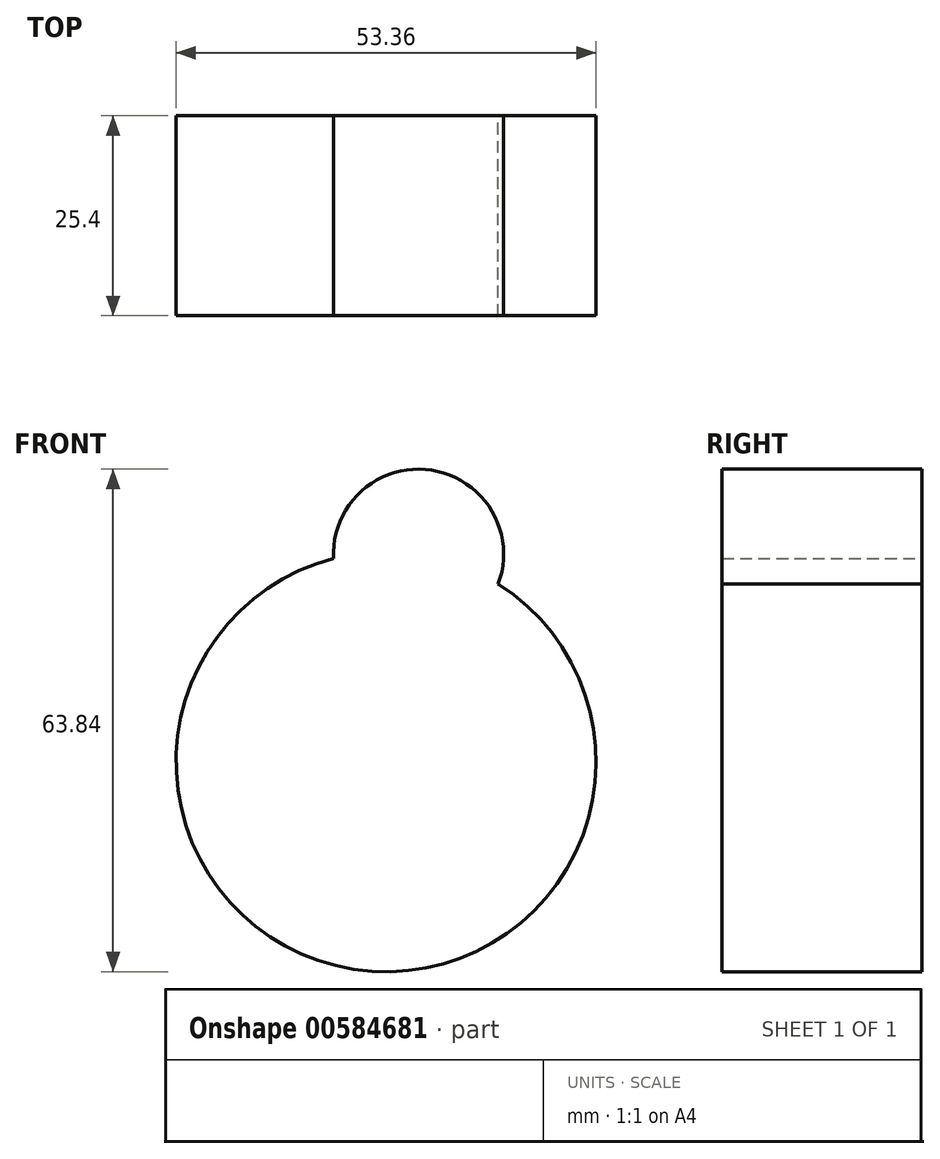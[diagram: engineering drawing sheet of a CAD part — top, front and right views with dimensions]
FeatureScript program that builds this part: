
annotation { "Feature Type Name" : "Feature", "Feature Type Description" : "" }
export const myFeature = defineFeature(function(context is Context, id is Id, definition is map)
    precondition{}
    {
        {
            var Q0;
            Q0=qCreatedBy(makeId("Front.planeOp"),FACE);
            var sketch = newSketch(context, id + "F0", { "sketchPlane" : qUnion([Q0])});
            skCircle(sketch, "E0", {"center": v(25.65, 22.03) * mm, "radius": 26.68 * mm});
            skCircle(sketch, "E1", {"center": v(29.76, 48.39) * mm, "radius": 10.8 * mm});
            skSolve(sketch);
        }
        {
            var Q0;
            Q0 = qSketchRegion(id + "F0", true);
            extrude(context, id + "F1", {"entities" : qUnion([Q0]), "depth" : 25.4 * mm, "offsetDistance" : 25.4 * mm});
        }
    });
